# Revit family: Grab_Bar-Grohe-Essentials-40421_Series
name_source: partatom
category: Specialty Equipment
revit_build: Autodesk Revit 2018 (Build: 20170223_1515(x64)
units: mm (PartAtom-declared; Revit-internal decimal feet)

## family parameters
Cut with Voids When Loaded = No
Host = Face
OmniClass Number = 23.40.20.21.47
OmniClass Title = Bath Grab Bars
Part Type = Normal
Room Calculation Point = No
Round Connector Dimension = Use Diameter
Shared = Yes

## types (5) — shared parameters
Assembly Code = C1030200
Default Elevation = 0"
Description = Essentials Grip Bar
Height = 2 1/8"
Installation Type = Wall Mounted
Length = 11 5/8"
Manufacturer = Grohe
Price = Prices may vary. Please consult Manufacturer Representative for most up-to-date price list.
Product Documentation Link = https://americanstandard.box.com
Product Page URL = https://www.grohe.us
Revised Date = 05/28/2021
URL = https://www.grohe.us
Warranty Information = Limited Lifetime Warranty
Width = 3 1/2"

## per-type parameters (varying)
| type | Finish | Material |
| 40421A01 | Metal-Grohe-A01-Hard Graphite | Metal-Grohe-A01-Hard Graphite |
| 40421BE1 | Metal-Grohe-BE1-Polished Nickel | Metal-Grohe-BE1-Polished Nickel |
| 40421GN1 | Metal-Grohe-GN1-Brushed Cool Sunset | Metal-Grohe-GN1-Brushed Cool Sunset |
| 40421EN1 | Metal-Grohe-EN1-Brushed Nickel Infinity Finish | Metal-Grohe-EN1-Brushed Nickel Infinity Finish |
| 40421001 | Metal-Grohe-001-StarLight Chrome | Metal-Grohe-001-StarLight Chrome |

note: column(s) folded — value = type name in every type: Model

## geometry (parser evidence)
native form markers: Sweep x3
no freeform markers — native parametric forms only
